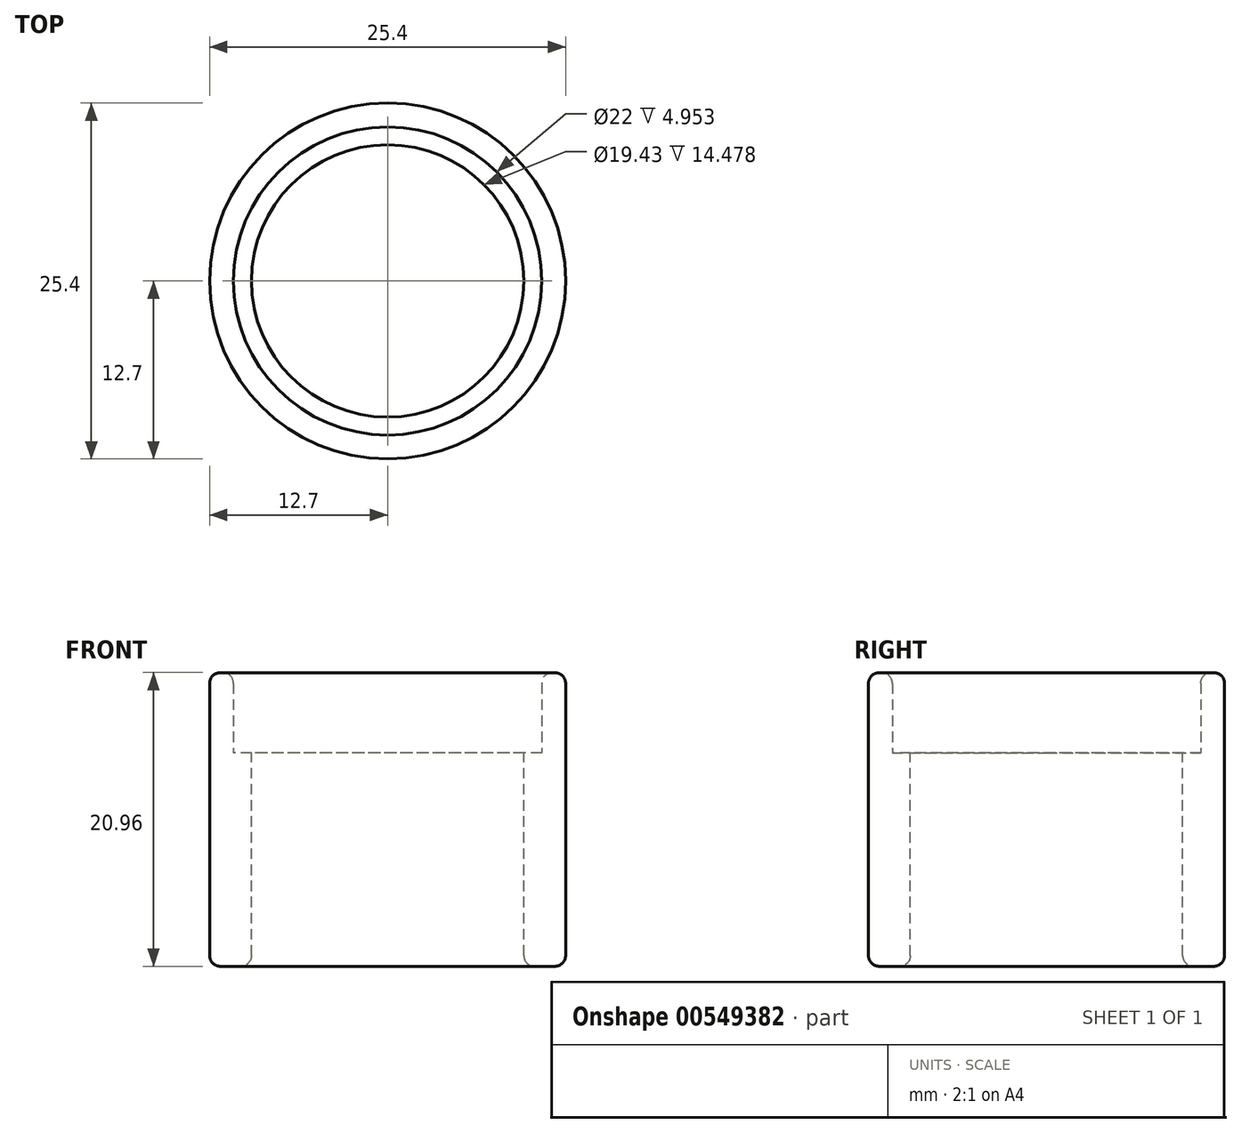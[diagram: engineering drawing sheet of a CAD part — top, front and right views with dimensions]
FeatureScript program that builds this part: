
annotation { "Feature Type Name" : "Feature", "Feature Type Description" : "" }
export const myFeature = defineFeature(function(context is Context, id is Id, definition is map)
    precondition{}
    {
        {
            var Q0;
            Q0=qCreatedBy(makeId("Top.planeOp"),FACE);
            var sketch = newSketch(context, id + "F0", { "sketchPlane" : qUnion([Q0])});
            skCircle(sketch, "E0", {"center": v(0, 0) * mm, "radius": 12.7 * mm});
            skCircle(sketch, "E1", {"center": v(0, 0) * mm, "radius": 9.72 * mm});
            skCircle(sketch, "E2", {"center": v(0, 0) * mm, "radius": 11 * mm});
            skSolve(sketch);
        }
        {
            var Q0;
            Q0=makeQuery(id+"F0.imprint","IMPRINT",FACE,{"disambiguationData":[TD([[makeQuery(id+"F0.imprint","IMPRINT",EDGE,{"derivedFrom":sQuery(id+"F0.wireOp",EDGE,"E0")}),1.0]])]});
            extrude(context, id + "F1", {"entities" : qUnion([Q0]), "depth" : 5.7 * mm, "offsetDistance" : 25.4 * mm});
        }
        {
            var Q0;
            Q0 = qSketchRegion(id + "F0", true);
            var Q1;
            Q1=makeQuery(id+"F0.imprint","IMPRINT",FACE,{"disambiguationData":[TD([[makeQuery(id+"F0.imprint","IMPRINT",EDGE,{"derivedFrom":sQuery(id+"F0.wireOp",EDGE,"E1")}),-1.0]])]});
            extrude(context, id + "F2", {"entities" : qUnion([Q0, Q1]), "operationType" : NewBodyOperationType.ADD, "oppositeDirection" : true, "depth" : 15.24 * mm, "offsetDistance" : 25.4 * mm});
        }
        {
            var Q0;
            Q0=makeQuery(id+"F2.opExtrude","CAP_EDGE",EDGE,{"disambiguationData":[OSD([sQuery(id+"F0.wireOp",EDGE,"E1")])],"isStart":false});
            var Q1;
            Q1=makeQuery(id+"F2.opExtrude","CAP_EDGE",EDGE,{"disambiguationData":[OSD([sQuery(id+"F0.wireOp",EDGE,"E0")])],"isStart":false});
            var Q2;
            Q2=makeQuery(id+"F1.opExtrude","CAP_EDGE",EDGE,{"disambiguationData":[OSD([sQuery(id+"F0.wireOp",EDGE,"E0")])],"isStart":false});
            var Q3;
            Q3=makeQuery(id+"F1.opExtrude","CAP_EDGE",EDGE,{"disambiguationData":[OSD([sQuery(id+"F0.wireOp",EDGE,"E2")])],"isStart":false});
            fillet(context, id + "F3", {"entities" : qUnion([Q0, Q1, Q2, Q3]), "radius" : 0.76 * mm, "tangentPropagation" : true, "allowEdgeOverflow" : false});
        }
    });
